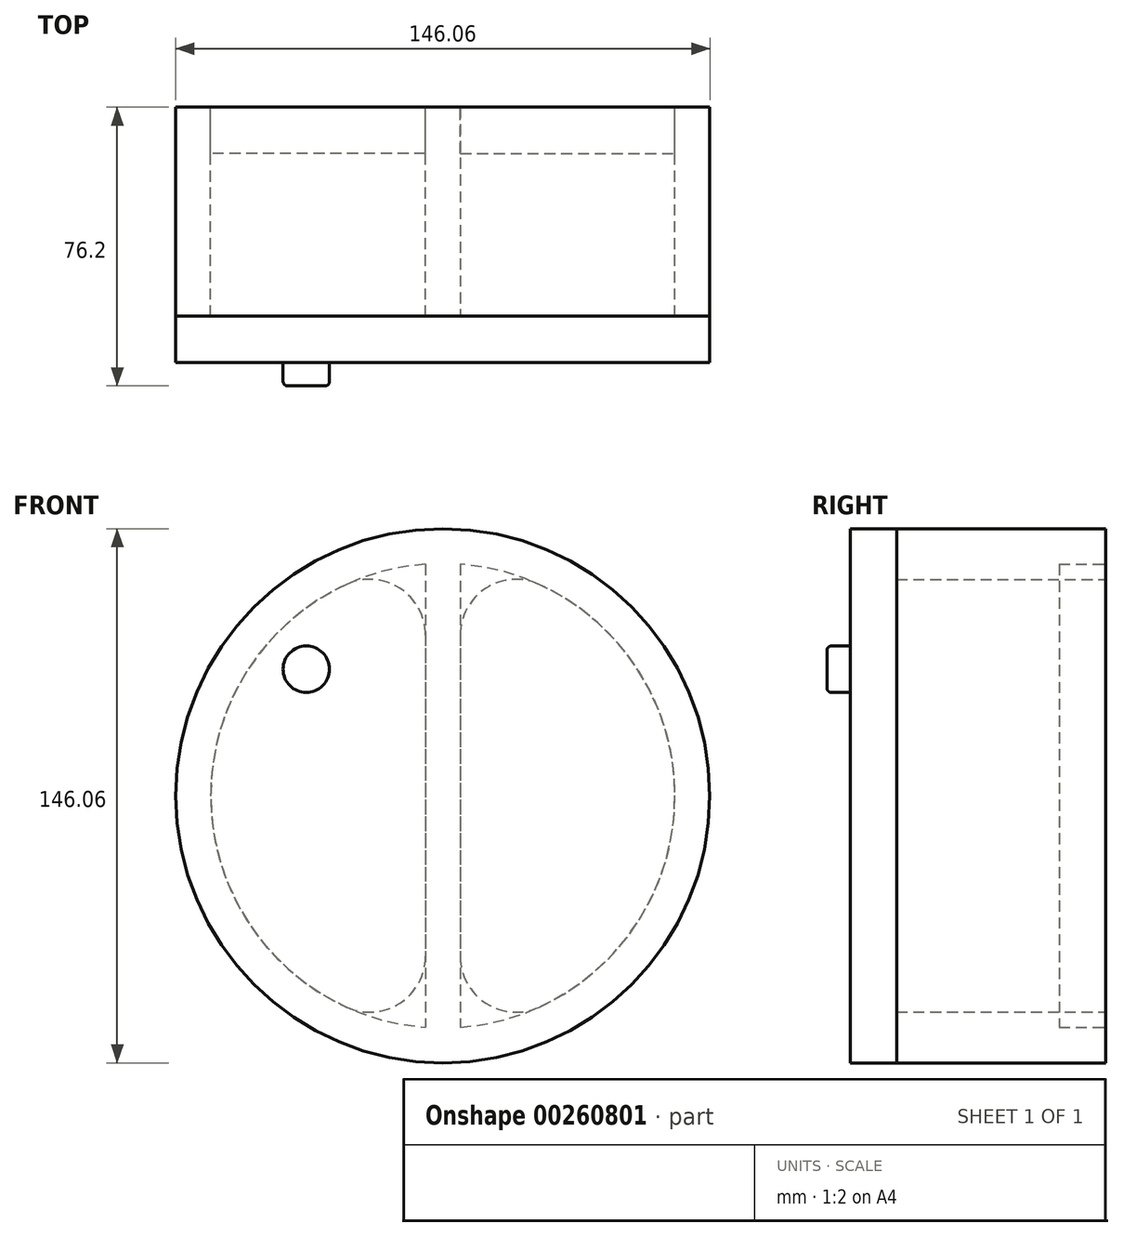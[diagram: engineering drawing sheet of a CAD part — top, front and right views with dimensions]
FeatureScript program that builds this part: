
annotation { "Feature Type Name" : "Feature", "Feature Type Description" : "" }
export const myFeature = defineFeature(function(context is Context, id is Id, definition is map)
    precondition{}
    {
        {
            var Q0;
            Q0=qCreatedBy(makeId("Front.planeOp"),FACE);
            var sketch = newSketch(context, id + "F0", { "sketchPlane" : qUnion([Q0])});
            skCircle(sketch, "E0", {"center": v(0, 0) * mm, "radius": 73.03 * mm});
            skCircle(sketch, "E1", {"center": v(0, 0) * mm, "radius": 63.5 * mm});
            skLineSegment(sketch, "E2", {"start": v(0, 0) * mm, "end": v(-4.76, 0) * mm});
            skLineSegment(sketch, "E3", {"start": v(0, 0) * mm, "end": v(4.76, 0) * mm});
            skLineSegment(sketch, "E4", {"start": v(-4.76, 63.32) * mm, "end": v(-4.76, -63.32) * mm});
            skLineSegment(sketch, "E5", {"start": v(4.76, 63.32) * mm, "end": v(4.76, -63.32) * mm});
            skSolve(sketch);
        }
        {
            var Q0;
            Q0=makeQuery(id+"F0.imprint","IMPRINT",FACE,{"disambiguationData":[TD([[makeQuery(id+"F0.imprint","IMPRINT",EDGE,{"derivedFrom":sQuery(id+"F0.wireOp",EDGE,"E0")}),1.0]])]});
            var Q1;
            {var subQ1=sQuery(id+"F0.wireOp",EDGE,"E2");Q1=makeQuery(id+"F0.imprint","IMPRINT",FACE,{"disambiguationData":[TD([[makeQuery(id+"F0.imprint","IMPRINT",EDGE,{"derivedFrom":subQ1}),-1.0]])]});}
            var Q2;
            {var subQ1=sQuery(id+"F0.wireOp",EDGE,"E2");Q2=makeQuery(id+"F0.imprint","IMPRINT",FACE,{"disambiguationData":[TD([[makeQuery(id+"F0.imprint","IMPRINT",EDGE,{"derivedFrom":subQ1}),1.0]])]});}
            extrude(context, id + "F1", {"entities" : qUnion([Q0, Q1, Q2]), "depth" : 57.15 * mm});
        }
        {
            var Q0;
            {var subQ0=sQuery(id+"F0.wireOp",EDGE,"E4");var subQ1=sQuery(id+"F0.wireOp",EDGE,"E1");var subQ2=makeQuery(id+"F0.imprint","INTERSECT",VERTEX,{"disambiguationData":[OD(0.0)],"derivedFrom":[subQ1,subQ0]});Q0=makeQuery(id+"F0.imprint","IMPRINT",FACE,{"disambiguationData":[TD([[makeQuery(id+"F0.imprint","IMPRINT",EDGE,{"disambiguationData":[TD([[subQ2,-1.0]])],"derivedFrom":subQ1}),1.0]])]});}
            var Q1;
            {var subQ0=sQuery(id+"F0.wireOp",EDGE,"E5");var subQ1=sQuery(id+"F0.wireOp",EDGE,"E1");var subQ2=makeQuery(id+"F0.imprint","INTERSECT",VERTEX,{"disambiguationData":[OD(0.0)],"derivedFrom":[subQ1,subQ0]});Q1=makeQuery(id+"F0.imprint","IMPRINT",FACE,{"disambiguationData":[TD([[makeQuery(id+"F0.imprint","IMPRINT",EDGE,{"disambiguationData":[TD([[subQ2,1.0]])],"derivedFrom":subQ1}),1.0]])]});}
            extrude(context, id + "F2", {"entities" : qUnion([Q0, Q1]), "depth" : 12.7 * mm});
        }
        {
            var Q0;
            {var subQ0=sQuery(id+"F0.wireOp",EDGE,"E4");var subQ1=sQuery(id+"F0.wireOp",EDGE,"E1");Q0=makeQuery(id+"F1.opExtrude","SWEPT_EDGE",EDGE,{"disambiguationData":[OSD([subQ1,subQ0]),TDD([makeQuery(id+"F0.imprint","INTERSECT",VERTEX,{"disambiguationData":[OD(0.0)],"derivedFrom":[subQ1,subQ0]})])]});}
            var Q1;
            {var subQ0=sQuery(id+"F0.wireOp",EDGE,"E5");var subQ1=sQuery(id+"F0.wireOp",EDGE,"E1");Q1=makeQuery(id+"F1.opExtrude","SWEPT_EDGE",EDGE,{"disambiguationData":[OSD([subQ1,subQ0]),TDD([makeQuery(id+"F0.imprint","INTERSECT",VERTEX,{"disambiguationData":[OD(0.0)],"derivedFrom":[subQ1,subQ0]})])]});}
            var Q2;
            {var subQ0=sQuery(id+"F0.wireOp",EDGE,"E5");var subQ1=sQuery(id+"F0.wireOp",EDGE,"E1");Q2=makeQuery(id+"F1.opExtrude","SWEPT_EDGE",EDGE,{"disambiguationData":[OSD([subQ1,subQ0]),TDD([makeQuery(id+"F0.imprint","INTERSECT",VERTEX,{"disambiguationData":[OD(1.0)],"derivedFrom":[subQ1,subQ0]})])]});}
            var Q3;
            {var subQ0=sQuery(id+"F0.wireOp",EDGE,"E4");var subQ1=sQuery(id+"F0.wireOp",EDGE,"E1");Q3=makeQuery(id+"F1.opExtrude","SWEPT_EDGE",EDGE,{"disambiguationData":[OSD([subQ1,subQ0]),TDD([makeQuery(id+"F0.imprint","INTERSECT",VERTEX,{"disambiguationData":[OD(1.0)],"derivedFrom":[subQ1,subQ0]})])]});}
            fillet(context, id + "F3", {"entities" : qUnion([Q0, Q1, Q2, Q3]), "radius" : 15.24 * mm, "tangentPropagation" : true, "allowEdgeOverflow" : false});
        }
        {
            var Q0;
            Q0=qCreatedBy(makeId("Front.planeOp"),FACE);
            cPlane(context, id + "F4", {"entities" : qUnion([Q0]), "cplaneType" : CPlaneType.OFFSET, "offset" : 57.15 * mm, "width" : 152.4 * mm, "height" : 152.4 * mm});
        }
        {
            var Q0;
            Q0=qCreatedBy(id+"F4.planeOp",FACE);
            var sketch = newSketch(context, id + "F5", { "sketchPlane" : qUnion([Q0])});
            skCircle(sketch, "E6", {"center": v(0, 0) * mm, "radius": 73.03 * mm});
            skSolve(sketch);
        }
        {
            var Q0;
            Q0 = qSketchRegion(id + "F5", true);
            extrude(context, id + "F6", {"entities" : qUnion([Q0]), "depth" : 12.7 * mm});
        }
        {
            var Q0;
            Q0=makeQuery(id+"F6.opExtrude","CAP_FACE",FACE,{"disambiguationData":[OSD([sQuery(id+"F5.wireOp",EDGE,"E6")])],"isStart":false});
            var sketch = newSketch(context, id + "F7", { "sketchPlane" : qUnion([Q0])});
            skCircle(sketch, "E7", {"center": v(-37.35, 34.6) * mm, "radius": 6.35 * mm});
            skSolve(sketch);
        }
        {
            var Q0;
            Q0=makeQuery(id+"F7.imprint","IMPRINT",FACE,{"disambiguationData":[TD([[makeQuery(id+"F7.imprint","IMPRINT",EDGE,{"derivedFrom":sQuery(id+"F7.wireOp",EDGE,"E7")}),1.0]])]});
            extrude(context, id + "F8", {"entities" : qUnion([Q0]), "operationType" : NewBodyOperationType.ADD, "depth" : 6.35 * mm});
        }
        {
            var Q0;
            Q0=makeQuery(id+"F8.opExtrude","CAP_EDGE",EDGE,{"disambiguationData":[OSD([sQuery(id+"F7.wireOp",EDGE,"E7")])],"isStart":false});
            fillet(context, id + "F9", {"entities" : qUnion([Q0]), "radius" : 1.27 * mm, "tangentPropagation" : true, "allowEdgeOverflow" : false});
        }
    });
